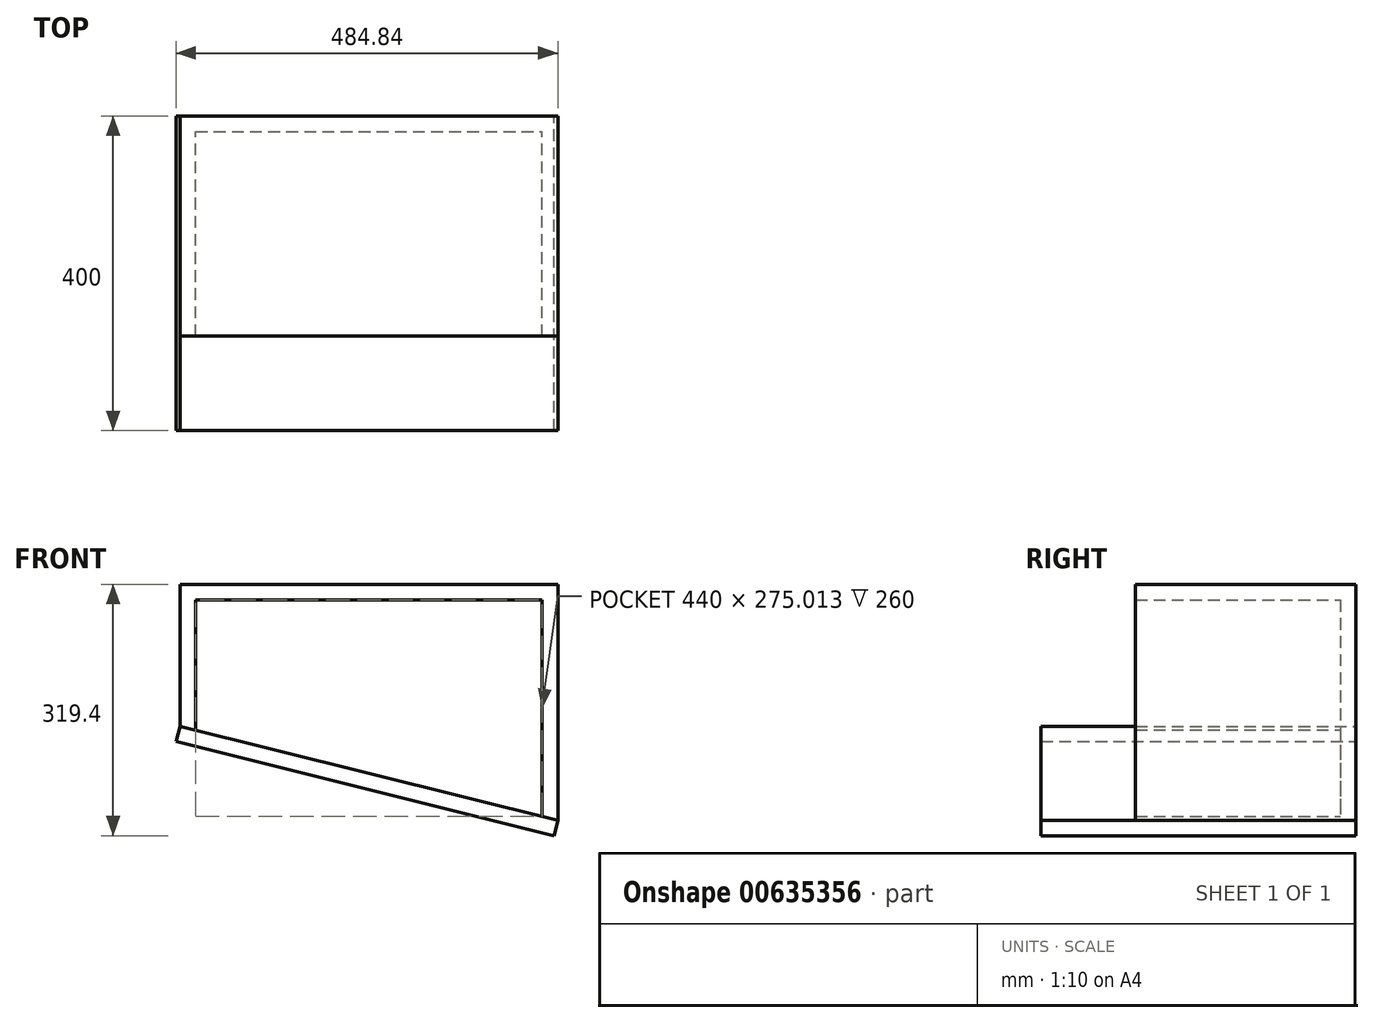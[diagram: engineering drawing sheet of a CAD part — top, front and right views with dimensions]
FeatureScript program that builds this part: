
annotation { "Feature Type Name" : "Feature", "Feature Type Description" : "" }
export const myFeature = defineFeature(function(context is Context, id is Id, definition is map)
    precondition{}
    {
        {
            var Q0;
            Q0=qCreatedBy(makeId("Front.planeOp"),FACE);
            var sketch = newSketch(context, id + "F0", { "sketchPlane" : qUnion([Q0])});
            skLineSegment(sketch, "E0.bottom", {"start": v(-5001.59, -1323.49) * mm, "end": v(-4521.59, -1323.49) * mm});
            skLineSegment(sketch, "E0.top", {"start": v(-5001.59, -1503.8) * mm, "end": v(-4521.59, -1623.49) * mm});
            skLineSegment(sketch, "E0.left", {"start": v(-5001.59, -1323.49) * mm, "end": v(-5001.59, -1503.8) * mm});
            skLineSegment(sketch, "E0.right", {"start": v(-4521.59, -1323.49) * mm, "end": v(-4521.59, -1623.49) * mm});
            skSolve(sketch);
        }
        {
            var Q0;
            Q0=makeQuery(id+"F0.imprint","IMPRINT",FACE,{"disambiguationData":[TD([[makeQuery(id+"F0.imprint","IMPRINT",EDGE,{"derivedFrom":sQuery(id+"F0.wireOp",EDGE,"E0.bottom")}),-1.0]])]});
            extrude(context, id + "F1", {"entities" : qUnion([Q0]), "depth" : 20 * mm, "offsetDistance" : 25.4 * mm});
        }
        {
            var Q0;
            Q0=makeQuery(id+"F1.opExtrude","CAP_FACE",FACE,{"disambiguationData":[OSD([sQuery(id+"F0.wireOp",EDGE,"E0.bottom"),sQuery(id+"F0.wireOp",EDGE,"E0.top"),sQuery(id+"F0.wireOp",EDGE,"E0.left"),sQuery(id+"F0.wireOp",EDGE,"E0.right")])],"isStart":false});
            var sketch = newSketch(context, id + "F2", { "sketchPlane" : qUnion([Q0])});
            skLineSegment(sketch, "E1.bottom", {"start": v(-5001.59, -1323.49) * mm, "end": v(-4521.59, -1323.49) * mm});
            skLineSegment(sketch, "E1.left", {"start": v(-5001.59, -1323.49) * mm, "end": v(-5001.59, -1503.8) * mm});
            skLineSegment(sketch, "E1.right", {"start": v(-4521.59, -1323.49) * mm, "end": v(-4521.59, -1623.49) * mm});
            skLineSegment(sketch, "E2.bottom", {"start": v(-4981.59, -1343.49) * mm, "end": v(-4541.59, -1343.49) * mm});
            skLineSegment(sketch, "E2.left", {"start": v(-4981.59, -1343.49) * mm, "end": v(-4981.59, -1508.8) * mm});
            skLineSegment(sketch, "E2.right", {"start": v(-4541.59, -1343.49) * mm, "end": v(-4541.59, -1618.5) * mm});
            skLineSegment(sketch, "E3", {"start": v(-5001.59, -1503.8) * mm, "end": v(-4981.59, -1508.8) * mm});
            skLineSegment(sketch, "E4", {"start": v(-4521.59, -1623.49) * mm, "end": v(-4541.59, -1618.5) * mm});
            skSolve(sketch);
        }
        {
            var Q0;
            Q0=makeQuery(id+"F2.imprint","IMPRINT",FACE,{"disambiguationData":[TD([[makeQuery(id+"F2.imprint","IMPRINT",EDGE,{"derivedFrom":sQuery(id+"F2.wireOp",EDGE,"E1.bottom")}),-1.0]])]});
            extrude(context, id + "F3", {"entities" : qUnion([Q0]), "operationType" : NewBodyOperationType.ADD, "depth" : 260 * mm, "offsetDistance" : 25.4 * mm});
        }
        {
            var Q0;
            Q0=makeQuery(id+"F1.opExtrude","CAP_FACE",FACE,{"disambiguationData":[OSD([sQuery(id+"F0.wireOp",EDGE,"E0.bottom"),sQuery(id+"F0.wireOp",EDGE,"E0.top"),sQuery(id+"F0.wireOp",EDGE,"E0.left"),sQuery(id+"F0.wireOp",EDGE,"E0.right")])],"isStart":true});
            var sketch = newSketch(context, id + "F4", { "sketchPlane" : qUnion([Q0])});
            skLineSegment(sketch, "E5", {"start": v(5001.59, -1503.8) * mm, "end": v(5006.43, -1523.21) * mm});
            skLineSegment(sketch, "E6", {"start": v(5006.43, -1523.21) * mm, "end": v(4526.43, -1642.9) * mm});
            skLineSegment(sketch, "E7", {"start": v(5001.59, -1503.8) * mm, "end": v(4521.59, -1623.49) * mm});
            skLineSegment(sketch, "E8", {"start": v(4521.59, -1623.49) * mm, "end": v(4526.43, -1642.9) * mm});
            skSolve(sketch);
        }
        {
            var Q0;
            Q0=makeQuery(id+"F4.imprint","IMPRINT",FACE,{"disambiguationData":[TD([[makeQuery(id+"F4.imprint","IMPRINT",EDGE,{"derivedFrom":sQuery(id+"F4.wireOp",EDGE,"E5")}),-1.0]])]});
            extrude(context, id + "F5", {"entities" : qUnion([Q0]), "operationType" : NewBodyOperationType.ADD, "oppositeDirection" : true, "depth" : 400 * mm, "offsetDistance" : 25.4 * mm});
        }
    });
